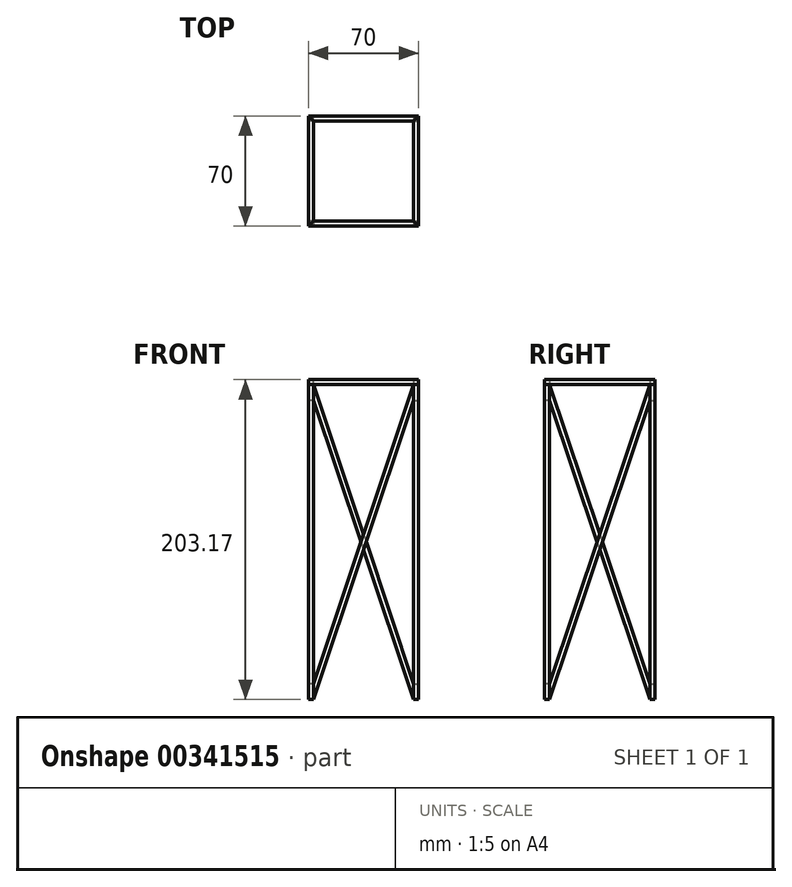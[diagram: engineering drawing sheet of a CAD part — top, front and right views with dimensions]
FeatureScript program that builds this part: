
annotation { "Feature Type Name" : "Feature", "Feature Type Description" : "" }
export const myFeature = defineFeature(function(context is Context, id is Id, definition is map)
    precondition{}
    {
        {
            var Q0;
            Q0=qCreatedBy(makeId("Front.planeOp"),FACE);
            var sketch = newSketch(context, id + "F0", { "sketchPlane" : qUnion([Q0])});
            skLineSegment(sketch, "E0.bottom", {"start": v(0, 200) * mm, "end": v(3.17, 200) * mm});
            skLineSegment(sketch, "E0.top", {"start": v(0, 0) * mm, "end": v(3.18, 0) * mm});
            skLineSegment(sketch, "E0.left", {"start": v(0, 200) * mm, "end": v(0, 0) * mm});
            skLineSegment(sketch, "E0.right", {"start": v(3.17, 200) * mm, "end": v(3.18, 0) * mm});
            skLineSegment(sketch, "E1.bottom", {"start": v(0, 203.18) * mm, "end": v(70, 203.18) * mm});
            skLineSegment(sketch, "E1.top", {"start": v(0, 200) * mm, "end": v(70, 200) * mm});
            skLineSegment(sketch, "E1.left", {"start": v(0, 203.18) * mm, "end": v(0, 200) * mm});
            skLineSegment(sketch, "E1.right", {"start": v(70, 203.18) * mm, "end": v(70, 200) * mm});
            skLineSegment(sketch, "E2", {"start": v(3.17, 200) * mm, "end": v(66.83, 10) * mm});
            skLineSegment(sketch, "E3", {"start": v(3.18, 200) * mm, "end": v(3.18, 190) * mm});
            skLineSegment(sketch, "E4", {"start": v(66.83, 0) * mm, "end": v(66.83, 10) * mm});
            skLineSegment(sketch, "E5", {"start": v(3.18, 190) * mm, "end": v(66.83, 0) * mm});
            skSolve(sketch);
        }
        {
            var Q0;
            Q0=makeQuery(id+"F0.imprint","IMPRINT",FACE,{"disambiguationData":[TD([[makeQuery(id+"F0.imprint","IMPRINT",EDGE,{"derivedFrom":sQuery(id+"F0.wireOp",EDGE,"E0.top")}),1.0]])]});
            extrude(context, id + "F1", {"entities" : qUnion([Q0]), "depth" : 3.17 * mm});
        }
        {
            var Q0;
            Q0=makeQuery(id+"F0.imprint","IMPRINT",FACE,{"disambiguationData":[TD([[makeQuery(id+"F0.imprint","IMPRINT",EDGE,{"derivedFrom":sQuery(id+"F0.wireOp",EDGE,"E1.bottom")}),-1.0]])]});
            extrude(context, id + "F2", {"entities" : qUnion([Q0]), "depth" : 3.17 * mm});
        }
        {
            var Q0;
            Q0=makeQuery(id+"F0.imprint","IMPRINT",FACE,{"disambiguationData":[TD([[makeQuery(id+"F0.imprint","IMPRINT",EDGE,{"derivedFrom":sQuery(id+"F0.wireOp",EDGE,"E2")}),-1.0]])]});
            var Q1;
            Q1=sQuery(id+"F0.wireOp",EDGE,"E2");
            extrude(context, id + "F3", {"entities" : qUnion([Q0]), "surfaceEntities" : qUnion([Q1]), "depth" : 3.17 * mm});
        }
        {
            var Q0;
            Q0=qCreatedBy(makeId("Front.planeOp"),FACE);
            cPlane(context, id + "F4", {"entities" : qUnion([Q0]), "cplaneType" : CPlaneType.OFFSET, "offset" : 35 * mm, "width" : 150 * mm, "height" : 150 * mm});
        }
        {
            var Q0;
            Q0=qCreatedBy(id+"F4.planeOp",FACE);
            var sketch = newSketch(context, id + "F5", { "sketchPlane" : qUnion([Q0])});
            skLineSegment(sketch, "E6", {"start": v(35, 200) * mm, "end": v(35, 0) * mm});
            skSolve(sketch);
        }
        {
            var Q0;
            Q0=makeQuery(id+"F2.opExtrude","CAP_EDGE",EDGE,{"disambiguationData":[OSD([sQuery(id+"F0.wireOp",EDGE,"E1.left")])],"isStart":false});
            var Q1;
            Q1=makeQuery(id+"F2.opExtrude","CAP_EDGE",EDGE,{"disambiguationData":[OSD([sQuery(id+"F0.wireOp",EDGE,"E1.right")])],"isStart":false});
            chamfer(context, id + "F6", {"entities" : qUnion([Q0, Q1]), "width" : 3.17 * mm, "tangentPropagation" : true});
        }
        {
            var Q0;
            Q0=makeQuery(id+"F1.opExtrude","SWEPT_BODY",BODY,{"disambiguationData":[OSD([sQuery(id+"F0.wireOp",EDGE,"E0.top"),sQuery(id+"F0.wireOp",EDGE,"E0.left"),sQuery(id+"F0.wireOp",EDGE,"E0.right"),sQuery(id+"F0.wireOp",EDGE,"E1.top")])]});
            var Q1;
            Q1=makeQuery(id+"F2.opExtrude","SWEPT_BODY",BODY,{"disambiguationData":[OSD([sQuery(id+"F0.wireOp",EDGE,"E1.bottom"),sQuery(id+"F0.wireOp",EDGE,"E1.top"),sQuery(id+"F0.wireOp",EDGE,"E1.left"),sQuery(id+"F0.wireOp",EDGE,"E1.right")])]});
            var Q2;
            Q2=makeQuery(id+"F3.opExtrude","SWEPT_BODY",BODY,{"disambiguationData":[OSD([sQuery(id+"F0.wireOp",EDGE,"E2"),sQuery(id+"F0.wireOp",EDGE,"E3"),sQuery(id+"F0.wireOp",EDGE,"E4"),sQuery(id+"F0.wireOp",EDGE,"E5")])]});
            var Q3;
            Q3=sQuery(id+"F5.wireOp",EDGE,"E6");
            transform(context, id + "F7", {"entities" : qUnion([Q0, Q1, Q2]), "transformType" : TransformType.ROTATION, "transformAxis" : qUnion([Q3]), "angle" : 90 * degree, "makeCopy" : true});
        }
        {
            var Q0;
            Q0=makeQuery(id+"F1.opExtrude","SWEPT_BODY",BODY,{"disambiguationData":[OSD([sQuery(id+"F0.wireOp",EDGE,"E0.top"),sQuery(id+"F0.wireOp",EDGE,"E0.left"),sQuery(id+"F0.wireOp",EDGE,"E0.right"),sQuery(id+"F0.wireOp",EDGE,"E1.top")])]});
            var Q1;
            Q1=makeQuery(id+"F2.opExtrude","SWEPT_BODY",BODY,{"disambiguationData":[OSD([sQuery(id+"F0.wireOp",EDGE,"E1.bottom"),sQuery(id+"F0.wireOp",EDGE,"E1.top"),sQuery(id+"F0.wireOp",EDGE,"E1.left"),sQuery(id+"F0.wireOp",EDGE,"E1.right")])]});
            var Q2;
            Q2=makeQuery(id+"F7.opPattern","COPY",BODY,{"derivedFrom":makeQuery(id+"F1.opExtrude","SWEPT_BODY",BODY,{"disambiguationData":[OSD([sQuery(id+"F0.wireOp",EDGE,"E0.top"),sQuery(id+"F0.wireOp",EDGE,"E0.left"),sQuery(id+"F0.wireOp",EDGE,"E0.right"),sQuery(id+"F0.wireOp",EDGE,"E1.top")])]}),"instanceName":"1"});
            var Q3;
            Q3=makeQuery(id+"F7.opPattern","COPY",BODY,{"derivedFrom":makeQuery(id+"F2.opExtrude","SWEPT_BODY",BODY,{"disambiguationData":[OSD([sQuery(id+"F0.wireOp",EDGE,"E1.bottom"),sQuery(id+"F0.wireOp",EDGE,"E1.top"),sQuery(id+"F0.wireOp",EDGE,"E1.left"),sQuery(id+"F0.wireOp",EDGE,"E1.right")])]}),"instanceName":"1"});
            var Q4;
            Q4=makeQuery(id+"F3.opExtrude","SWEPT_BODY",BODY,{"disambiguationData":[OSD([sQuery(id+"F0.wireOp",EDGE,"E2"),sQuery(id+"F0.wireOp",EDGE,"E3"),sQuery(id+"F0.wireOp",EDGE,"E4"),sQuery(id+"F0.wireOp",EDGE,"E5")])]});
            var Q5;
            Q5=makeQuery(id+"F7.opPattern","COPY",BODY,{"derivedFrom":makeQuery(id+"F3.opExtrude","SWEPT_BODY",BODY,{"disambiguationData":[OSD([sQuery(id+"F0.wireOp",EDGE,"E2"),sQuery(id+"F0.wireOp",EDGE,"E3"),sQuery(id+"F0.wireOp",EDGE,"E4"),sQuery(id+"F0.wireOp",EDGE,"E5")])]}),"instanceName":"1"});
            var Q6;
            Q6=sQuery(id+"F5.wireOp",EDGE,"E6");
            transform(context, id + "F8", {"entities" : qUnion([Q0, Q1, Q2, Q3, Q4, Q5]), "transformType" : TransformType.ROTATION, "transformAxis" : qUnion([Q6]), "angle" : 180 * degree, "makeCopy" : true});
        }
    });
